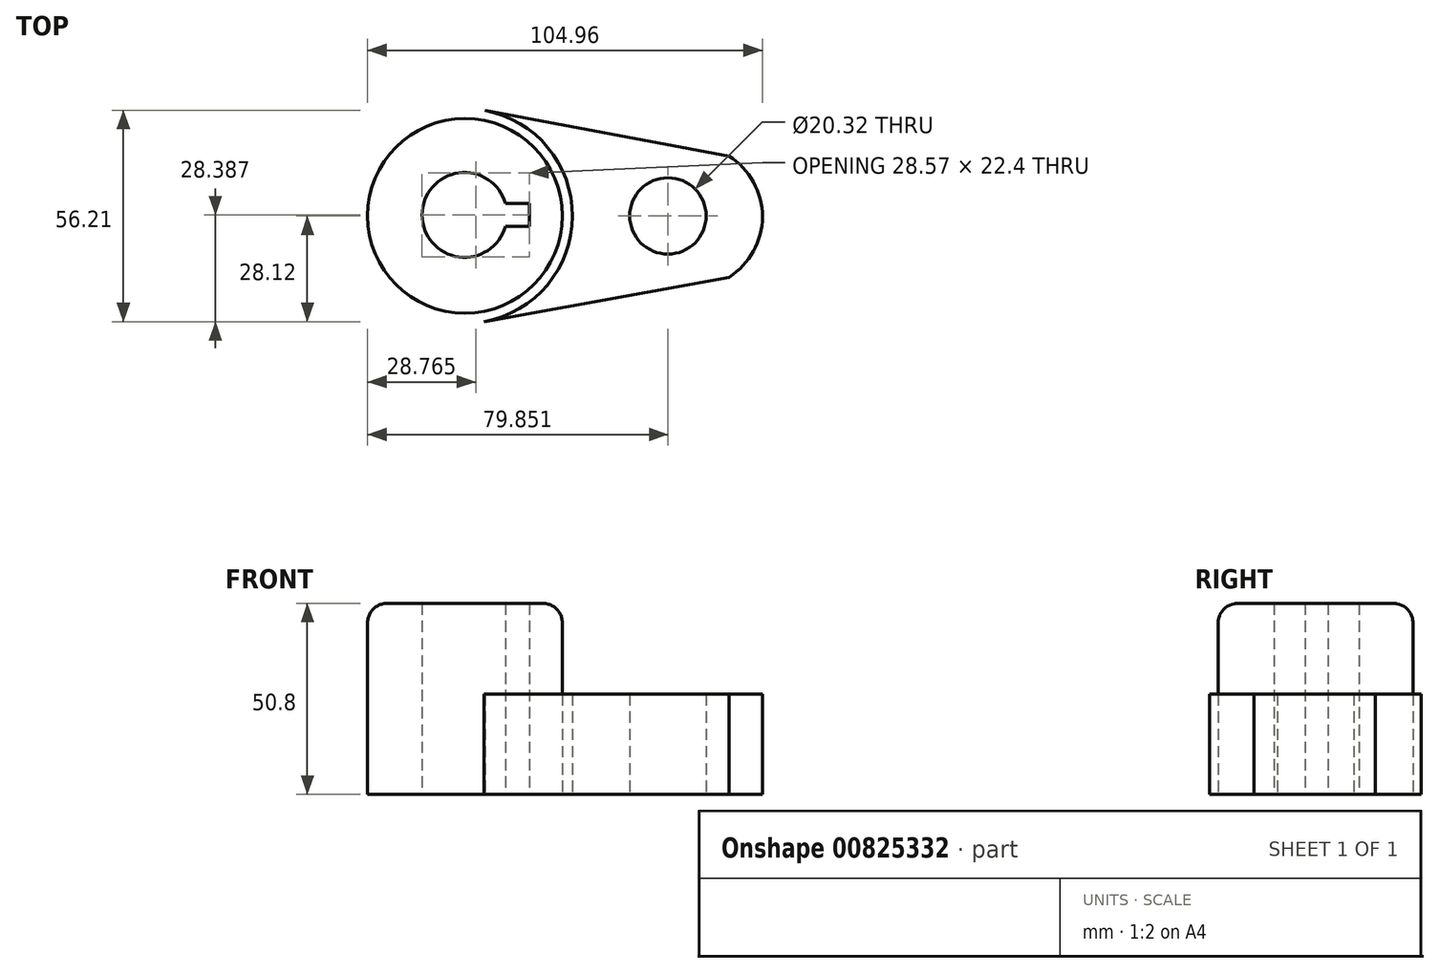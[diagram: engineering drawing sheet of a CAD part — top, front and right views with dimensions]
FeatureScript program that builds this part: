
annotation { "Feature Type Name" : "Feature", "Feature Type Description" : "" }
export const myFeature = defineFeature(function(context is Context, id is Id, definition is map)
    precondition{}
    {
        {
            var Q0;
            Q0=qCreatedBy(makeId("Top.planeOp"),FACE);
            var sketch = newSketch(context, id + "F0", { "sketchPlane" : qUnion([Q0])});
            skCircle(sketch, "E0", {"center": v(16.23, 0) * mm, "radius": 10.16 * mm});
            skArc(sketch, "E1", {"start": v(32.47, -16.3) * mm, "mid": v(41.34, -0.2) * mm, "end": v(32.47, 15.9) * mm});
            skCircle(sketch, "E2", {"center": v(-37.74, 0) * mm, "radius": 25.88 * mm});
            skLineSegment(sketch, "E3", {"start": v(32.47, -16.3) * mm, "end": v(-32.64, -28.12) * mm});
            skLineSegment(sketch, "E4", {"start": v(32.47, 15.9) * mm, "end": v(-32.48, 28.09) * mm});
            skLineSegment(sketch, "E5", {"start": v(-26.96, 3.33) * mm, "end": v(-20.57, 3.33) * mm});
            skLineSegment(sketch, "E6", {"start": v(-26.96, -2.8) * mm, "end": v(-20.57, -2.8) * mm});
            skLineSegment(sketch, "E7", {"start": v(-20.57, -2.8) * mm, "end": v(-20.57, 3.33) * mm});
            skArc(sketch, "E8", {"start": v(-26.96, 3.33) * mm, "mid": v(-49.14, 0.27) * mm, "end": v(-26.96, -2.8) * mm});
            skArc(sketch, "E9", {"start": v(-32.64, -28.12) * mm, "mid": v(-9.17, -0.08) * mm, "end": v(-32.48, 28.09) * mm});
            skSolve(sketch);
        }
        {
            var Q0;
            Q0=makeQuery(id+"F0.imprint","IMPRINT",FACE,{"disambiguationData":[TD([[makeQuery(id+"F0.imprint","IMPRINT",EDGE,{"derivedFrom":sQuery(id+"F0.wireOp",EDGE,"E2")}),1.0]])]});
            var Q1;
            Q1=makeQuery(id+"F0.imprint","IMPRINT",FACE,{"disambiguationData":[TD([[makeQuery(id+"F0.imprint","IMPRINT",EDGE,{"derivedFrom":sQuery(id+"F0.wireOp",EDGE,"E0")}),-1.0]])]});
            extrude(context, id + "F1", {"entities" : qUnion([Q0, Q1]), "depth" : 50.8 * mm, "offsetDistance" : 25.4 * mm});
        }
        {
            var Q0;
            Q0=makeQuery(id+"F1.opExtrude","CAP_FACE",FACE,{"disambiguationData":[OSD([sQuery(id+"F0.wireOp",EDGE,"E0"),sQuery(id+"F0.wireOp",EDGE,"E1"),sQuery(id+"F0.wireOp",EDGE,"E3"),sQuery(id+"F0.wireOp",EDGE,"E4"),sQuery(id+"F0.wireOp",EDGE,"E9")])],"isStart":false});
            extrude(context, id + "F2", {"entities" : qUnion([Q0]), "operationType" : NewBodyOperationType.REMOVE, "oppositeDirection" : true, "depth" : 24.13 * mm, "offsetDistance" : 25.4 * mm});
        }
        {
            var Q0;
            Q0=makeQuery(id+"F1.opExtrude","CAP_EDGE",EDGE,{"disambiguationData":[OSD([sQuery(id+"F0.wireOp",EDGE,"E2")])],"isStart":false});
            fillet(context, id + "F3", {"entities" : qUnion([Q0]), "radius" : 5.08 * mm, "tangentPropagation" : true, "allowEdgeOverflow" : false});
        }
    });
